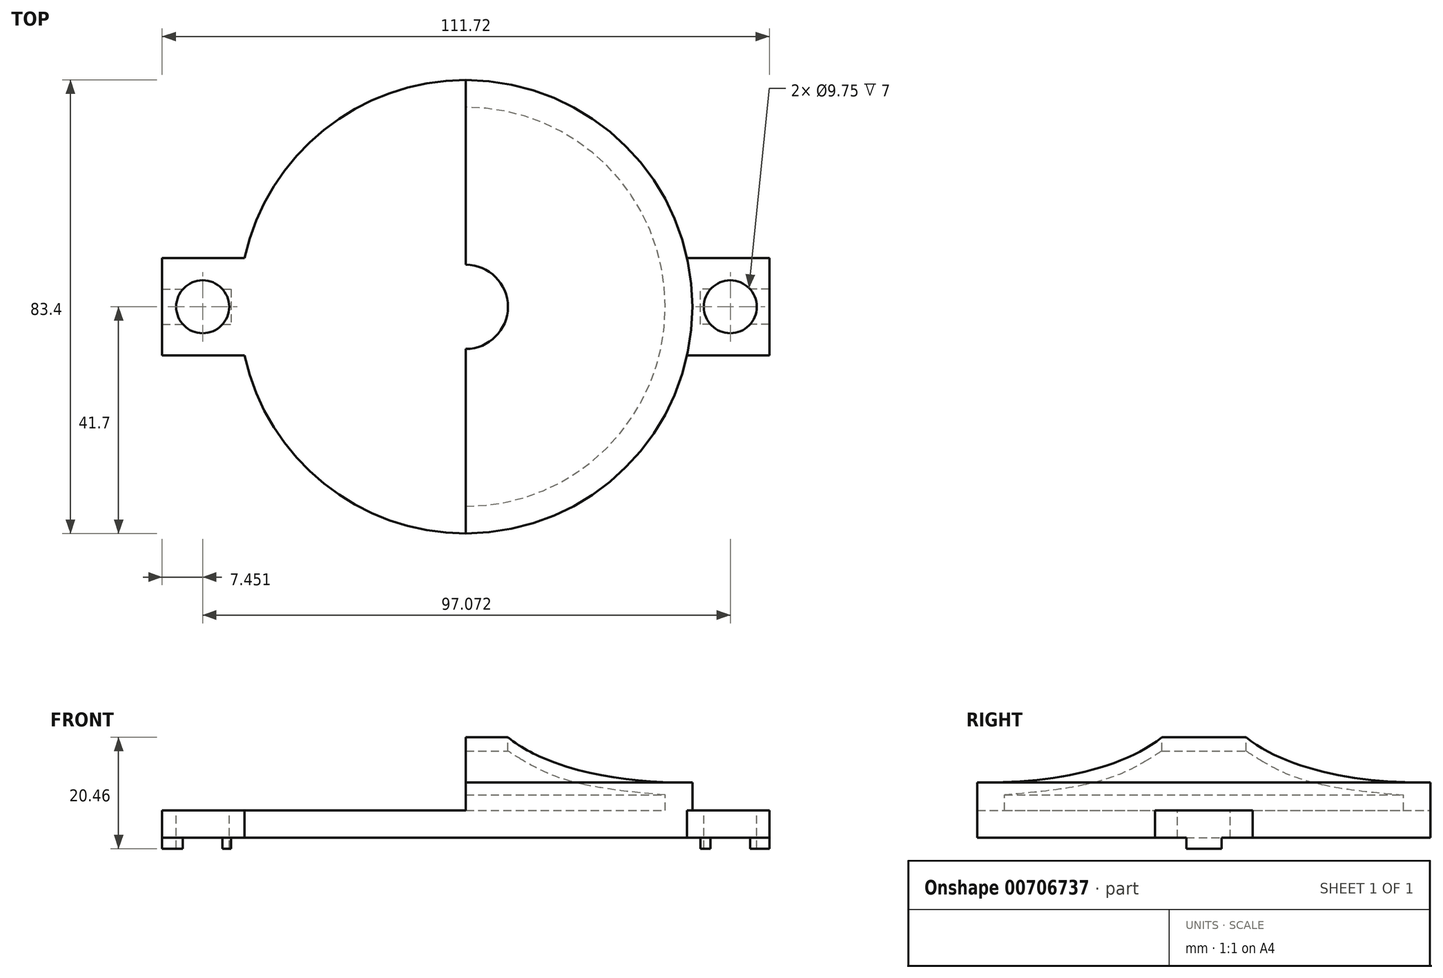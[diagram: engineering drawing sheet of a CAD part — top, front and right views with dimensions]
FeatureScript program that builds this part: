
annotation { "Feature Type Name" : "Feature", "Feature Type Description" : "" }
export const myFeature = defineFeature(function(context is Context, id is Id, definition is map)
    precondition{}
    {
        {
            var Q0;
            Q0=qCreatedBy(makeId("Front.planeOp"),FACE);
            var sketch = newSketch(context, id + "F0", { "sketchPlane" : qUnion([Q0])});
            skLineSegment(sketch, "E0", {"start": v(0, 0) * mm, "end": v(41.7, 0) * mm});
            skLineSegment(sketch, "E1", {"start": v(7.75, 18.46) * mm, "end": v(7.75, 15.96) * mm});
            skLineSegment(sketch, "E2", {"start": v(36.7, 7.9) * mm, "end": v(36.7, 5) * mm});
            skLineSegment(sketch, "E3", {"start": v(36.7, 5) * mm, "end": v(0, 5) * mm});
            skLineSegment(sketch, "E4", {"start": v(0, 5) * mm, "end": v(0, 0) * mm});
            skFitSpline(sketch, "E5", {"points": [v(7.75, 15.96) * mm, v(36.7, 7.9) * mm], "startDerivative": vector(20.3, -12.9) * mm, "endDerivative": vector(54.63, -3.9) * mm});
            skFitSpline(sketch, "E6", {"points": [v(7.75, 18.46) * mm, v(41.7, 10.16) * mm], "startDerivative": vector(22.81, -18.07) * mm, "endDerivative": vector(39.57, 0.66) * mm});
            skLineSegment(sketch, "E7", {"start": v(41.7, 10.16) * mm, "end": v(41.7, 0) * mm});
            skLineSegment(sketch, "E8", {"start": v(21.7, 9.8) * mm, "end": v(21.7, 5) * mm});
            skLineSegment(sketch, "E9", {"start": v(10.4, 14.3) * mm, "end": v(10.4, 5) * mm});
            skSolve(sketch);
        }
        {
            var Q0;
            Q0=makeQuery(id+"F0.imprint","IMPRINT",FACE,{"disambiguationData":[TD([[makeQuery(id+"F0.imprint","IMPRINT",EDGE,{"derivedFrom":sQuery(id+"F0.wireOp",EDGE,"E0")}),1.0]])]});
            var Q1;
            Q1=sQuery(id+"F0.wireOp",EDGE,"E4");
            revolve(context, id + "F1", {"surfaceOperationType" : NewSurfaceOperationType.NEW, "entities" : qUnion([Q0]), "axis" : qUnion([Q1]), "revolveType" : RevolveType.FULL});
        }
        {
            var Q0;
            Q0=qCreatedBy(makeId("Front.planeOp"),FACE);
            var sketch = newSketch(context, id + "F2", { "sketchPlane" : qUnion([Q0])});
            skLineSegment(sketch, "E10", {"start": v(0, 50.87) * mm, "end": v(0, 5) * mm});
            skLineSegment(sketch, "E11", {"start": v(0, 5) * mm, "end": v(-90.82, 5) * mm});
            skLineSegment(sketch, "E12", {"start": v(-90.82, 5) * mm, "end": v(-90.82, 44.19) * mm});
            skLineSegment(sketch, "E13", {"start": v(-90.82, 44.19) * mm, "end": v(0, 50.87) * mm});
            skLineSegment(sketch, "E14", {"start": v(0, 0) * mm, "end": v(0, 55.78) * mm});
            skSolve(sketch);
        }
        {
            var Q0;
            Q0 = qSketchRegion(id + "F2", true);
            extrude(context, id + "F3", {"entities" : qUnion([Q0]), "operationType" : NewBodyOperationType.REMOVE, "endBound" : BoundingType.SYMMETRIC, "depth" : 101.6 * mm, "offsetDistance" : 25.4 * mm});
        }
        {
            var Q0;
            Q0=qCreatedBy(makeId("Top.planeOp"),FACE);
            var sketch = newSketch(context, id + "F4", { "sketchPlane" : qUnion([Q0])});
            skLineSegment(sketch, "E15", {"start": v(0, 4.7) * mm, "end": v(-12.84, 12.1) * mm});
            skLineSegment(sketch, "E16", {"start": v(-12.84, 12.1) * mm, "end": v(-12.84, -12.1) * mm});
            skLineSegment(sketch, "E17", {"start": v(-12.84, -12.1) * mm, "end": v(0, -4.7) * mm});
            skLineSegment(sketch, "E18", {"start": v(0, 4.7) * mm, "end": v(0, -4.7) * mm});
            skSolve(sketch);
        }
        {
            var Q0;
            Q0 = qSketchRegion(id + "F4", true);
            extrude(context, id + "F5", {"entities" : qUnion([Q0]), "operationType" : NewBodyOperationType.REMOVE, "depth" : 25.4 * mm, "offsetDistance" : 25.4 * mm});
        }
        {
            var Q0;
            Q0=makeQuery(id+"F1.opRevolve","SWEPT_FACE",FACE,{"disambiguationData":[OSD([sQuery(id+"F0.wireOp",EDGE,"E0")])]});
            var sketch = newSketch(context, id + "F6", { "sketchPlane" : qUnion([Q0])});
            skLineSegment(sketch, "E19", {"start": v(0, 4.7) * mm, "end": v(0, -4.7) * mm});
            skLineSegment(sketch, "E20", {"start": v(0, -4.7) * mm, "end": v(-12.84, -12.1) * mm});
            skLineSegment(sketch, "E21", {"start": v(-12.84, -12.1) * mm, "end": v(-12.84, 12.1) * mm});
            skLineSegment(sketch, "E22", {"start": v(-12.84, 12.1) * mm, "end": v(0, 4.7) * mm});
            skSolve(sketch);
        }
        {
            var Q0;
            Q0 = qSketchRegion(id + "F6", true);
            extrude(context, id + "F7", {"entities" : qUnion([Q0]), "operationType" : NewBodyOperationType.ADD, "oppositeDirection" : true, "depth" : 5 * mm, "offsetDistance" : 25.4 * mm});
        }
        {
            var Q0;
            Q0=makeQuery(id+"F7.boolean.opBoolean","MERGE",FACE,{"derivedFrom":[makeQuery(id+"F1.opRevolve","SWEPT_FACE",FACE,{"disambiguationData":[OSD([sQuery(id+"F0.wireOp",EDGE,"E0")])]}),makeQuery(id+"F7.opExtrude","CAP_FACE",FACE,{"disambiguationData":[OSD([sQuery(id+"F6.wireOp",EDGE,"E19"),sQuery(id+"F6.wireOp",EDGE,"E20"),sQuery(id+"F6.wireOp",EDGE,"E21"),sQuery(id+"F6.wireOp",EDGE,"E22")])],"isStart":true})]});
            var sketch = newSketch(context, id + "F8", { "sketchPlane" : qUnion([Q0])});
            skLineSegment(sketch, "E23.bottom", {"start": v(-55.86, 8.97) * mm, "end": v(-40.72, 8.97) * mm});
            skLineSegment(sketch, "E23.top", {"start": v(-55.86, -8.97) * mm, "end": v(-40.72, -8.97) * mm});
            skLineSegment(sketch, "E23.left", {"start": v(-55.86, 8.97) * mm, "end": v(-55.86, -8.97) * mm});
            skLineSegment(sketch, "E23.right", {"start": v(55.86, 8.97) * mm, "end": v(55.86, -8.97) * mm});
            skPoint(sketch, "E23.middle", {"position": v(0, 0) * mm});
            skLineSegment(sketch, "E24", {"start": v(-40.72, -8.97) * mm, "end": v(-40.72, 8.97) * mm});
            skLineSegment(sketch, "E25", {"start": v(40.72, -8.97) * mm, "end": v(40.72, 8.97) * mm});
            skLineSegment(sketch, "E26.trimOffspring", {"start": v(40.72, 8.97) * mm, "end": v(55.86, 8.97) * mm});
            skLineSegment(sketch, "E27.trimOffspring", {"start": v(40.72, -8.97) * mm, "end": v(55.86, -8.97) * mm});
            skSolve(sketch);
        }
        {
            var Q0;
            Q0 = qSketchRegion(id + "F8", true);
            extrude(context, id + "F9", {"entities" : qUnion([Q0]), "operationType" : NewBodyOperationType.ADD, "oppositeDirection" : true, "depth" : 5 * mm, "offsetDistance" : 25.4 * mm});
        }
        {
            var Q0;
            Q0=makeQuery(id+"F9.boolean.opBoolean","MERGE",FACE,{"derivedFrom":[makeQuery(id+"F7.boolean.opBoolean","MERGE",FACE,{"derivedFrom":[makeQuery(id+"F1.opRevolve","SWEPT_FACE",FACE,{"disambiguationData":[OSD([sQuery(id+"F0.wireOp",EDGE,"E0")])]}),makeQuery(id+"F7.opExtrude","CAP_FACE",FACE,{"disambiguationData":[OSD([sQuery(id+"F6.wireOp",EDGE,"E19"),sQuery(id+"F6.wireOp",EDGE,"E20"),sQuery(id+"F6.wireOp",EDGE,"E21"),sQuery(id+"F6.wireOp",EDGE,"E22")])],"isStart":true})]}),makeQuery(id+"F9.opExtrude","CAP_FACE",FACE,{"disambiguationData":[OSD([sQuery(id+"F8.wireOp",EDGE,"E23.bottom"),sQuery(id+"F8.wireOp",EDGE,"E23.top"),sQuery(id+"F8.wireOp",EDGE,"E23.left"),sQuery(id+"F8.wireOp",EDGE,"E24")])],"isStart":true}),makeQuery(id+"F9.opExtrude","CAP_FACE",FACE,{"disambiguationData":[OSD([sQuery(id+"F8.wireOp",EDGE,"E23.right"),sQuery(id+"F8.wireOp",EDGE,"E25"),sQuery(id+"F8.wireOp",EDGE,"E26.trimOffspring"),sQuery(id+"F8.wireOp",EDGE,"E27.trimOffspring")])],"isStart":true})]});
            var sketch = newSketch(context, id + "F10", { "sketchPlane" : qUnion([Q0])});
            skLineSegment(sketch, "E28", {"start": v(0, 0) * mm, "end": v(65.46, 0) * mm});
            skLineSegment(sketch, "E29", {"start": v(0, 0) * mm, "end": v(-58.36, 0) * mm});
            skLineSegment(sketch, "E30.bottom", {"start": v(-55.86, -3.24) * mm, "end": v(-43.16, -3.24) * mm});
            skLineSegment(sketch, "E30.top", {"start": v(-55.86, 3.24) * mm, "end": v(-43.16, 3.24) * mm});
            skLineSegment(sketch, "E30.left", {"start": v(-55.86, -3.24) * mm, "end": v(-55.86, 3.24) * mm});
            skLineSegment(sketch, "E30.right", {"start": v(-43.16, -3.24) * mm, "end": v(-43.16, 3.24) * mm});
            skLineSegment(sketch, "E31.bottom", {"start": v(55.86, 3.24) * mm, "end": v(43.16, 3.24) * mm});
            skLineSegment(sketch, "E31.top", {"start": v(55.86, -3.24) * mm, "end": v(43.16, -3.24) * mm});
            skLineSegment(sketch, "E31.left", {"start": v(55.86, 3.24) * mm, "end": v(55.86, -3.24) * mm});
            skLineSegment(sketch, "E31.right", {"start": v(43.16, 3.24) * mm, "end": v(43.16, -3.24) * mm});
            skSolve(sketch);
        }
        {
            var Q0;
            Q0 = qSketchRegion(id + "F10", true);
            extrude(context, id + "F11", {"entities" : qUnion([Q0]), "operationType" : NewBodyOperationType.ADD, "depth" : 2 * mm, "offsetDistance" : 25.4 * mm});
        }
        {
            var Q0;
            Q0=makeQuery(id+"F9.boolean.opBoolean","MERGE",FACE,{"derivedFrom":[makeQuery(id+"F7.boolean.opBoolean","MERGE",FACE,{"derivedFrom":[makeQuery(id+"F3.boolean.opBoolean","MERGE",FACE,{"derivedFrom":[makeQuery(id+"F1.opRevolve","SWEPT_FACE",FACE,{"disambiguationData":[OSD([sQuery(id+"F0.wireOp",EDGE,"E3")])]}),makeQuery(id+"F3.opExtrude","SWEPT_FACE",FACE,{"disambiguationData":[OSD([sQuery(id+"F2.wireOp",EDGE,"E11")])]})]}),makeQuery(id+"F7.opExtrude","CAP_FACE",FACE,{"disambiguationData":[OSD([sQuery(id+"F6.wireOp",EDGE,"E19"),sQuery(id+"F6.wireOp",EDGE,"E20"),sQuery(id+"F6.wireOp",EDGE,"E21"),sQuery(id+"F6.wireOp",EDGE,"E22")])],"isStart":false})]}),makeQuery(id+"F9.opExtrude","CAP_FACE",FACE,{"disambiguationData":[OSD([sQuery(id+"F8.wireOp",EDGE,"E23.bottom"),sQuery(id+"F8.wireOp",EDGE,"E23.top"),sQuery(id+"F8.wireOp",EDGE,"E23.left"),sQuery(id+"F8.wireOp",EDGE,"E24")])],"isStart":false})]});
            var sketch = newSketch(context, id + "F12", { "sketchPlane" : qUnion([Q0])});
            skCircle(sketch, "E32", {"center": v(-48.4, 0) * mm, "radius": 4.87 * mm});
            skCircle(sketch, "E33", {"center": v(48.66, 0) * mm, "radius": 4.87 * mm});
            skLineSegment(sketch, "E34", {"start": v(55.72, 0) * mm, "end": v(41.6, 0) * mm});
            skLineSegment(sketch, "E35", {"start": v(-55.86, 0) * mm, "end": v(-40.96, 0) * mm});
            skSolve(sketch);
        }
        {
            var Q0;
            Q0 = qSketchRegion(id + "F12", true);
            extrude(context, id + "F13", {"entities" : qUnion([Q0]), "operationType" : NewBodyOperationType.REMOVE, "oppositeDirection" : true, "depth" : 25.4 * mm, "offsetDistance" : 25.4 * mm});
        }
    });
